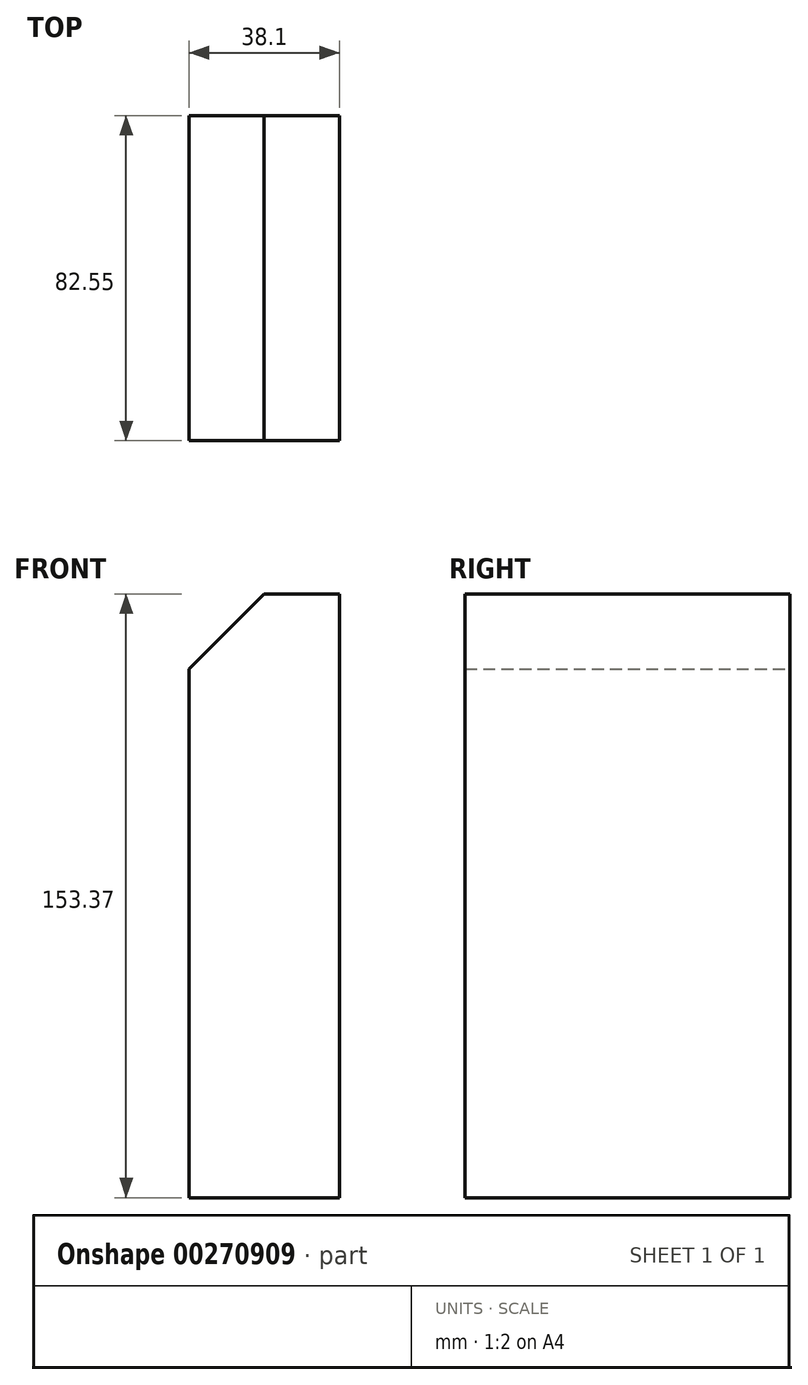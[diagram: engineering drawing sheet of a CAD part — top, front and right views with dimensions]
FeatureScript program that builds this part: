
annotation { "Feature Type Name" : "Feature", "Feature Type Description" : "" }
export const myFeature = defineFeature(function(context is Context, id is Id, definition is map)
    precondition{}
    {
        {
            var Q0;
            Q0=qCreatedBy(makeId("Front.planeOp"),FACE);
            var sketch = newSketch(context, id + "F0", { "sketchPlane" : qUnion([Q0])});
            skLineSegment(sketch, "E0.bottom", {"start": v(0, 0) * mm, "end": v(38.1, 0) * mm});
            skLineSegment(sketch, "E0.right", {"start": v(38.1, 0) * mm, "end": v(38.1, 153.37) * mm});
            skLineSegment(sketch, "E1", {"start": v(0, 0) * mm, "end": v(0, 134.32) * mm});
            skLineSegment(sketch, "E2", {"start": v(0, 134.32) * mm, "end": v(19.05, 153.37) * mm});
            skPoint(sketch, "E3.orphan", {"position": v(0, 153.37) * mm});
            skLineSegment(sketch, "E4", {"start": v(19.05, 153.37) * mm, "end": v(38.1, 153.37) * mm});
            skSolve(sketch);
        }
        {
            var Q0;
            Q0=makeQuery(id+"F0.imprint","IMPRINT",FACE,{"disambiguationData":[TD([[makeQuery(id+"F0.imprint","IMPRINT",EDGE,{"derivedFrom":sQuery(id+"F0.wireOp",EDGE,"E0.bottom")}),1.0]])]});
            extrude(context, id + "F1", {"entities" : qUnion([Q0]), "depth" : 82.55 * mm});
        }
    });
